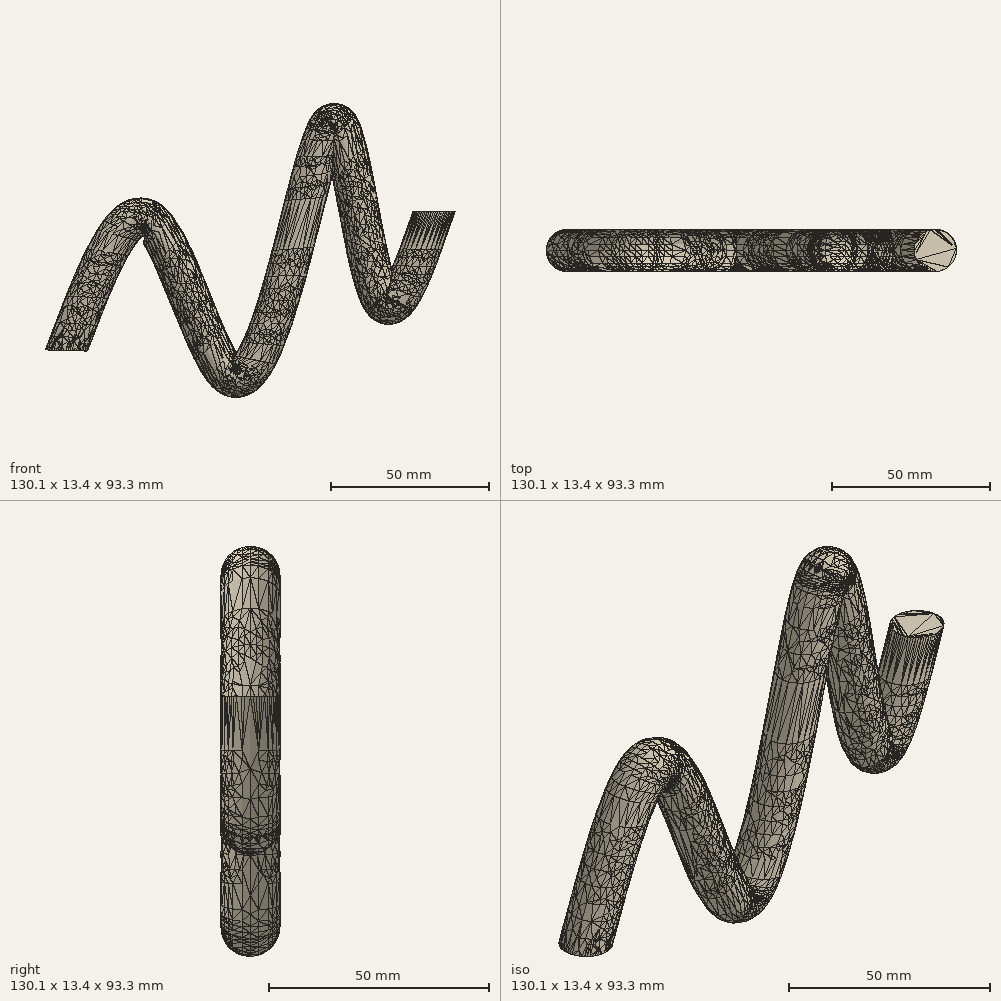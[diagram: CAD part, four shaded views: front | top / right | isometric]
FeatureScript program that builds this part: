
annotation { "Feature Type Name" : "Feature", "Feature Type Description" : "" }
export const myFeature = defineFeature(function(context is Context, id is Id, definition is map)
    precondition{}
    {
        {
            var Q0;
            Q0=qCreatedBy(makeId("Front.planeOp"),FACE);
            var sketch = newSketch(context, id + "F0", { "sketchPlane" : qUnion([Q0])});
            skFitSpline(sketch, "E0", {"points": [v(-56.2, -25.81) * mm, v(-30.24, 15.26) * mm, v(-4.28, -33.52) * mm, v(15.69, 6.42) * mm, v(29.95, 45.21) * mm, v(44.5, -10.13) * mm, v(60.47, 18.4) * mm], "startDerivative": vector(153.4, 407.06) * mm, "endDerivative": vector(122.64, 355.09) * mm});
            skSolve(sketch);
        }
        {
            var Q0;
            Q0=qCreatedBy(makeId("Top.planeOp"),FACE);
            var Q1;
            Q1=sQuery(id+"F0.wireOp",VERTEX,"E0.6.internal");
            cPlane(context, id + "F1", {"entities" : qUnion([Q0, Q1]), "cplaneType" : CPlaneType.PLANE_POINT, "offset" : 25.4 * mm, "width" : 152.4 * mm, "height" : 152.4 * mm});
        }
        {
            var Q0;
            Q0=qCreatedBy(id+"F1.planeOp",FACE);
            var sketch = newSketch(context, id + "F2", { "sketchPlane" : qUnion([Q0])});
            skCircle(sketch, "E1", {"center": v(60.47, 0) * mm, "radius": 6.71 * mm});
            skSolve(sketch);
        }
        {
            var Q0;
            Q0=makeQuery(id+"F2.imprint","IMPRINT",FACE,{"disambiguationData":[TD([[makeQuery(id+"F2.imprint","IMPRINT",EDGE,{"derivedFrom":sQuery(id+"F2.wireOp",EDGE,"E1")}),1.0]])]});
            var Q1;
            Q1=sQuery(id+"F0.wireOp",EDGE,"E0");
            sweep(context, id + "F3", {"profiles" : qUnion([Q0]), "path" : qUnion([Q1])});
        }
    });
